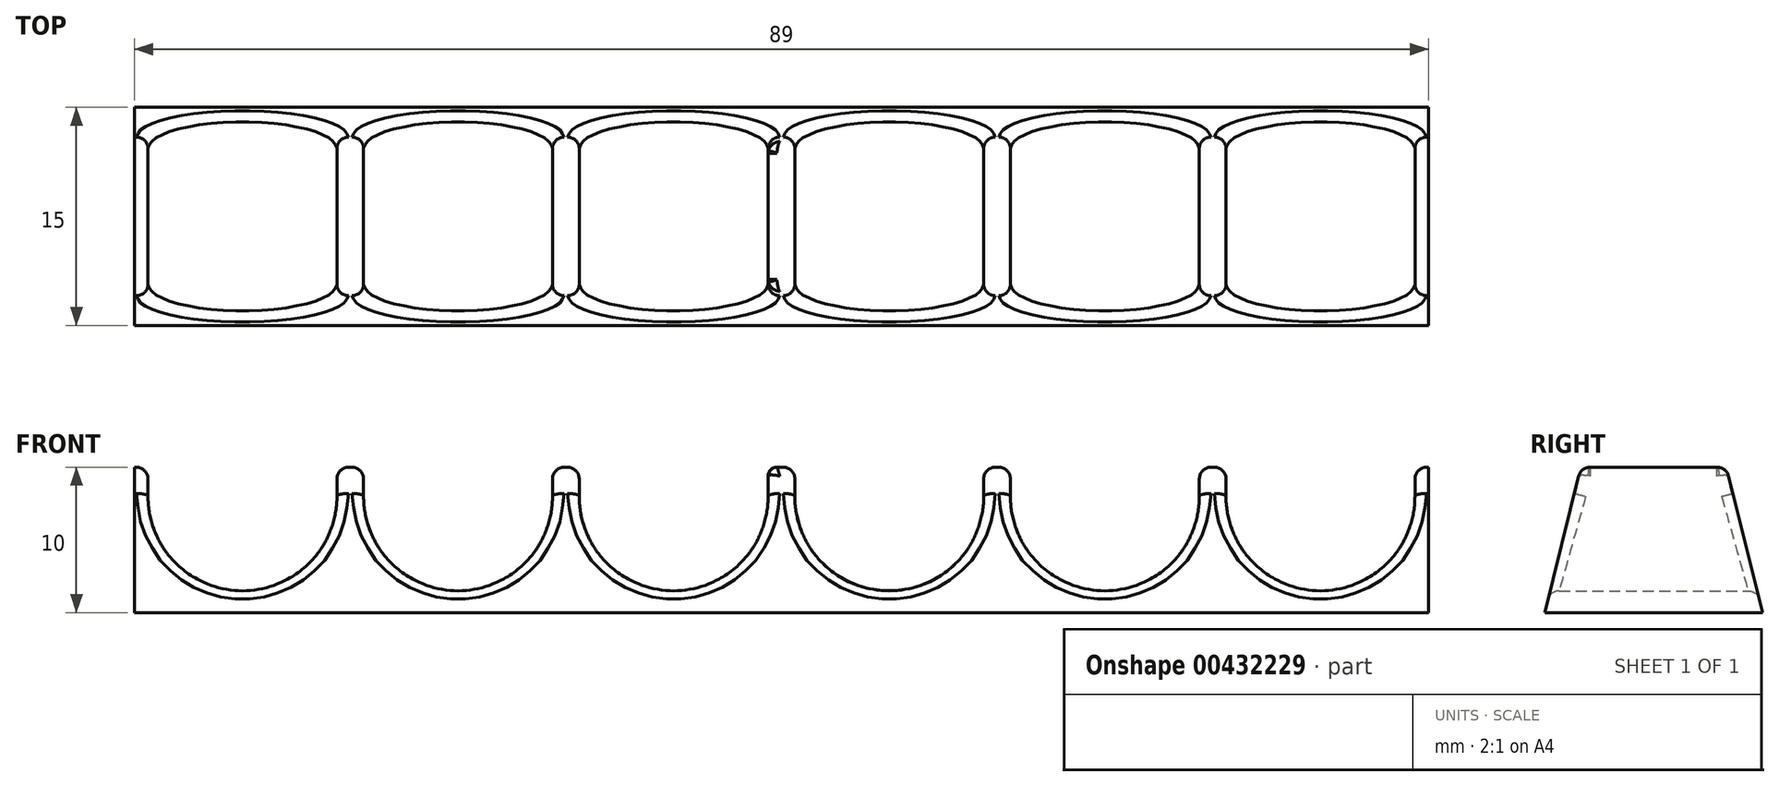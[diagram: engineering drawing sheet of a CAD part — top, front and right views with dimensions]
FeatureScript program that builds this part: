
annotation { "Feature Type Name" : "Feature", "Feature Type Description" : "" }
export const myFeature = defineFeature(function(context is Context, id is Id, definition is map)
    precondition{}
    {
        {
            var Q0;
            Q0=qCreatedBy(makeId("Front.planeOp"),FACE);
            var sketch = newSketch(context, id + "F0", { "sketchPlane" : qUnion([Q0])});
            skLineSegment(sketch, "E0.bottom", {"start": v(44.5, 5) * mm, "end": v(44.38, 5) * mm});
            skLineSegment(sketch, "E0.top", {"start": v(44.5, -5) * mm, "end": v(-44.5, -5) * mm});
            skLineSegment(sketch, "E0.left", {"start": v(44.5, 5) * mm, "end": v(44.5, -5) * mm});
            skLineSegment(sketch, "E0.right", {"start": v(-44.5, 5) * mm, "end": v(-44.5, -5) * mm});
            skPoint(sketch, "E0.middle", {"position": v(0, 0) * mm});
            skArc(sketch, "E1", {"start": v(-43.59, 3) * mm, "mid": v(-37.09, -3.5) * mm, "end": v(-30.59, 3) * mm});
            skLineSegment(sketch, "E2", {"start": v(-43.59, 3) * mm, "end": v(-43.59, 4.2) * mm});
            skLineSegment(sketch, "E3", {"start": v(-30.59, 3) * mm, "end": v(-30.59, 4.2) * mm});
            skLineSegment(sketch, "E4.trimOffspring", {"start": v(-44.38, 5) * mm, "end": v(-44.5, 5) * mm});
            skArc(sketch, "E5.1.0.0", {"start": v(-28.75, 3) * mm, "mid": v(-22.25, -3.5) * mm, "end": v(-15.75, 3) * mm});
            skLineSegment(sketch, "E5.1.0.1", {"start": v(-15.75, 3) * mm, "end": v(-15.75, 4.2) * mm});
            skLineSegment(sketch, "E5.1.0.2", {"start": v(-28.75, 3) * mm, "end": v(-28.75, 4.2) * mm});
            skArc(sketch, "E5.2.0.0", {"start": v(-13.92, 3) * mm, "mid": v(-7.42, -3.5) * mm, "end": v(-0.92, 3) * mm});
            skLineSegment(sketch, "E5.2.0.1", {"start": v(-0.92, 3) * mm, "end": v(-0.92, 4.4) * mm});
            skLineSegment(sketch, "E5.2.0.2", {"start": v(-13.92, 3) * mm, "end": v(-13.92, 4.2) * mm});
            skArc(sketch, "E5.3.0.0", {"start": v(0.91, 3) * mm, "mid": v(7.41, -3.5) * mm, "end": v(13.91, 3) * mm});
            skLineSegment(sketch, "E5.3.0.1", {"start": v(13.91, 3) * mm, "end": v(13.91, 4.2) * mm});
            skLineSegment(sketch, "E5.3.0.2", {"start": v(0.91, 3) * mm, "end": v(0.91, 4.2) * mm});
            skArc(sketch, "E5.4.0.0", {"start": v(15.75, 3) * mm, "mid": v(22.25, -3.5) * mm, "end": v(28.75, 3) * mm});
            skLineSegment(sketch, "E5.4.0.1", {"start": v(28.75, 3) * mm, "end": v(28.75, 4.2) * mm});
            skLineSegment(sketch, "E5.4.0.2", {"start": v(15.75, 3) * mm, "end": v(15.75, 4.2) * mm});
            skArc(sketch, "E5.5.0.0", {"start": v(30.58, 3) * mm, "mid": v(37.08, -3.5) * mm, "end": v(43.58, 3) * mm});
            skLineSegment(sketch, "E5.5.0.1", {"start": v(43.58, 3) * mm, "end": v(43.58, 4.2) * mm});
            skLineSegment(sketch, "E5.5.0.2", {"start": v(30.58, 3) * mm, "end": v(30.58, 4.2) * mm});
            skLineSegment(sketch, "E5.direction1", {"start": v(-43.59, 3) * mm, "end": v(-28.75, 3) * mm, "construction": true});
            skLineSegment(sketch, "E6.trimOffspring", {"start": v(-29.55, 5) * mm, "end": v(-29.79, 5) * mm});
            skLineSegment(sketch, "E7.trimOffspring", {"start": v(-14.72, 5) * mm, "end": v(-14.95, 5) * mm});
            skLineSegment(sketch, "E8.trimOffspring", {"start": v(0.11, 5) * mm, "end": v(-0.32, 5) * mm});
            skLineSegment(sketch, "E9.trimOffspring", {"start": v(14.95, 5) * mm, "end": v(14.71, 5) * mm});
            skLineSegment(sketch, "E10.trimOffspring", {"start": v(29.78, 5) * mm, "end": v(29.55, 5) * mm});
            skPoint(sketch, "E11.visualSharp", {"position": v(43.58, 5) * mm});
            skArc(sketch, "E11.filletArc", {"start": v(44.38, 5) * mm, "mid": v(43.81, 4.77) * mm, "end": v(43.58, 4.2) * mm});
            skPoint(sketch, "E12.visualSharp", {"position": v(30.58, 5) * mm});
            skArc(sketch, "E12.filletArc", {"start": v(30.58, 4.2) * mm, "mid": v(30.35, 4.77) * mm, "end": v(29.78, 5) * mm});
            skPoint(sketch, "E13.visualSharp", {"position": v(28.75, 5) * mm});
            skArc(sketch, "E13.filletArc", {"start": v(29.55, 5) * mm, "mid": v(28.98, 4.77) * mm, "end": v(28.75, 4.2) * mm});
            skPoint(sketch, "E14.visualSharp", {"position": v(15.75, 5) * mm});
            skArc(sketch, "E14.filletArc", {"start": v(15.75, 4.2) * mm, "mid": v(15.51, 4.77) * mm, "end": v(14.95, 5) * mm});
            skPoint(sketch, "E15.visualSharp", {"position": v(13.91, 5) * mm});
            skArc(sketch, "E15.filletArc", {"start": v(14.71, 5) * mm, "mid": v(14.15, 4.77) * mm, "end": v(13.91, 4.2) * mm});
            skPoint(sketch, "E16.visualSharp", {"position": v(0.91, 5) * mm});
            skArc(sketch, "E16.filletArc", {"start": v(0.91, 4.2) * mm, "mid": v(0.68, 4.77) * mm, "end": v(0.11, 5) * mm});
            skPoint(sketch, "E17.visualSharp", {"position": v(-0.92, 5) * mm});
            skArc(sketch, "E17.filletArc", {"start": v(-0.32, 5) * mm, "mid": v(-0.74, 4.82) * mm, "end": v(-0.92, 4.4) * mm});
            skPoint(sketch, "E18.visualSharp", {"position": v(-13.92, 5) * mm});
            skArc(sketch, "E18.filletArc", {"start": v(-13.92, 4.2) * mm, "mid": v(-14.15, 4.77) * mm, "end": v(-14.72, 5) * mm});
            skPoint(sketch, "E19.visualSharp", {"position": v(-15.75, 5) * mm});
            skArc(sketch, "E19.filletArc", {"start": v(-14.95, 5) * mm, "mid": v(-15.52, 4.77) * mm, "end": v(-15.75, 4.2) * mm});
            skPoint(sketch, "E20.visualSharp", {"position": v(-28.75, 5) * mm});
            skArc(sketch, "E20.filletArc", {"start": v(-28.75, 4.2) * mm, "mid": v(-28.99, 4.77) * mm, "end": v(-29.55, 5) * mm});
            skPoint(sketch, "E21.visualSharp", {"position": v(-30.59, 5) * mm});
            skArc(sketch, "E21.filletArc", {"start": v(-29.79, 5) * mm, "mid": v(-30.35, 4.77) * mm, "end": v(-30.59, 4.2) * mm});
            skPoint(sketch, "E22.visualSharp", {"position": v(-43.59, 5) * mm});
            skArc(sketch, "E22.filletArc", {"start": v(-43.59, 4.2) * mm, "mid": v(-43.82, 4.77) * mm, "end": v(-44.38, 5) * mm});
            skSolve(sketch);
        }
        {
            var Q0;
            Q0 = qSketchRegion(id + "F0", true);
            extrude(context, id + "F1", {"entities" : qUnion([Q0]), "depth" : 15 * mm});
        }
        {
            var Q0;
            Q0=makeQuery(id+"F1.opExtrude","SWEPT_FACE",FACE,{"disambiguationData":[OSD([sQuery(id+"F0.wireOp",EDGE,"E0.left")])]});
            var sketch = newSketch(context, id + "F2", { "sketchPlane" : qUnion([Q0])});
            skLineSegment(sketch, "E23", {"start": v(-15, 5) * mm, "end": v(-12.5, 5) * mm});
            skLineSegment(sketch, "E24", {"start": v(0, 5) * mm, "end": v(-2.5, 5) * mm});
            skLineSegment(sketch, "E25", {"start": v(-15, -5) * mm, "end": v(-15, 5) * mm});
            skLineSegment(sketch, "E26", {"start": v(-12.5, 5) * mm, "end": v(-15, -5) * mm});
            skLineSegment(sketch, "E27", {"start": v(-2.5, 5) * mm, "end": v(0, -5) * mm});
            skLineSegment(sketch, "E28", {"start": v(0, -5) * mm, "end": v(0, 5) * mm});
            skSolve(sketch);
        }
        {
            var Q0;
            Q0 = qSketchRegion(id + "F2", true);
            extrude(context, id + "F3", {"entities" : qUnion([Q0]), "operationType" : NewBodyOperationType.REMOVE, "endBound" : BoundingType.THROUGH_ALL, "oppositeDirection" : true, "depth" : 25 * mm});
        }
        {
            var Q0;
            Q0=makeQuery(id+"F3.boolean.opBoolean","INTERSECT",EDGE,{"derivedFrom":[makeQuery(id+"F1.opExtrude","SWEPT_FACE",FACE,{"disambiguationData":[OSD([sQuery(id+"F0.wireOp",EDGE,"E1")])]}),makeQuery(id+"F3.opExtrude","SWEPT_FACE",FACE,{"disambiguationData":[OSD([sQuery(id+"F2.wireOp",EDGE,"E26")])]})]});
            var Q1;
            Q1=makeQuery(id+"F3.boolean.opBoolean","INTERSECT",EDGE,{"derivedFrom":[makeQuery(id+"F1.opExtrude","SWEPT_FACE",FACE,{"disambiguationData":[OSD([sQuery(id+"F0.wireOp",EDGE,"E5.2.0.0")])]}),makeQuery(id+"F3.opExtrude","SWEPT_FACE",FACE,{"disambiguationData":[OSD([sQuery(id+"F2.wireOp",EDGE,"E27")])]})]});
            fillet(context, id + "F4", {"entities" : qUnion([Q0, Q1]), "radius" : .8 * mm, "tangentPropagation" : true, "allowEdgeOverflow" : false});
        }
    });
